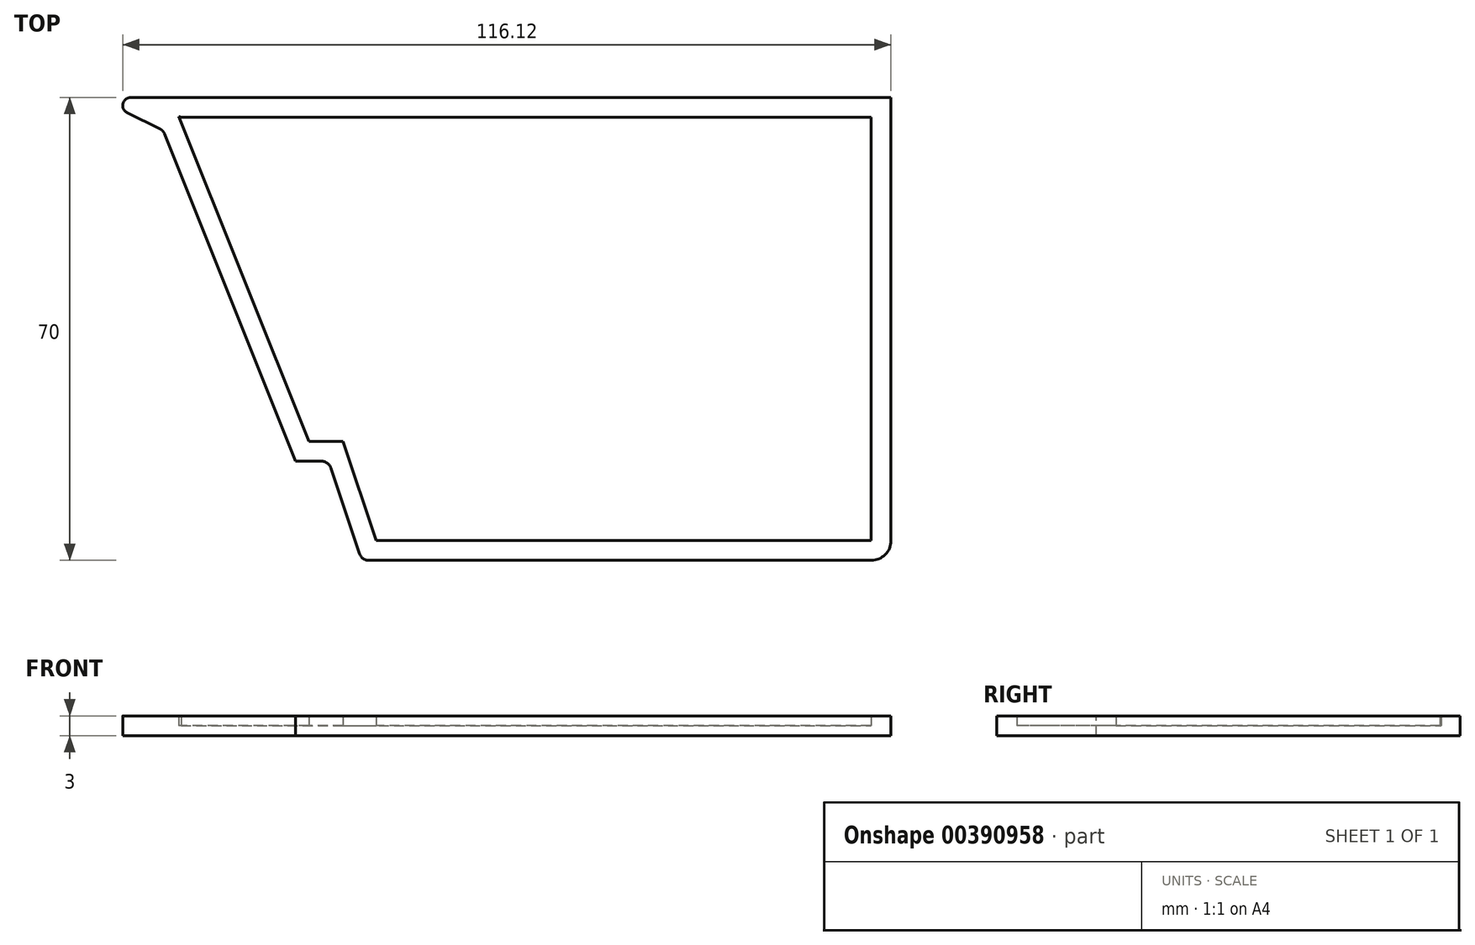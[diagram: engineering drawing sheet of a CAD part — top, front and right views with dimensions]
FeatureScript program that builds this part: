
annotation { "Feature Type Name" : "Feature", "Feature Type Description" : "" }
export const myFeature = defineFeature(function(context is Context, id is Id, definition is map)
    precondition{}
    {
        {
            var Q0;
            Q0=qCreatedBy(makeId("Top.planeOp"),FACE);
            var sketch = newSketch(context, id + "F0", { "sketchPlane" : qUnion([Q0])});
            skLineSegment(sketch, "E0.bottom", {"start": v(40, 35) * mm, "end": v(-40, 35) * mm});
            skLineSegment(sketch, "E0.top", {"start": v(40, -35) * mm, "end": v(-40, -35) * mm});
            skLineSegment(sketch, "E0.left", {"start": v(40, 35) * mm, "end": v(40, -35) * mm});
            skPoint(sketch, "E0.middle", {"position": v(0, 0) * mm});
            skLineSegment(sketch, "E1", {"start": v(-40, -35) * mm, "end": v(-45, -35) * mm, "construction": true});
            skLineSegment(sketch, "E2", {"start": v(-45, -35) * mm, "end": v(-45, -20) * mm, "construction": true});
            skLineSegment(sketch, "E3", {"start": v(-45, -20) * mm, "end": v(-40, -35) * mm});
            skLineSegment(sketch, "E4", {"start": v(-40, -35) * mm, "end": v(-70, -35) * mm, "construction": true});
            skLineSegment(sketch, "E5", {"start": v(-70, -35) * mm, "end": v(-70, 30) * mm, "construction": true});
            skLineSegment(sketch, "E6", {"start": v(-70, -35) * mm, "end": v(-80, -35) * mm, "construction": true});
            skLineSegment(sketch, "E7", {"start": v(-80, -35) * mm, "end": v(-80, 35) * mm, "construction": true});
            skLineSegment(sketch, "E8", {"start": v(-70, 30) * mm, "end": v(-80, 35) * mm});
            skLineSegment(sketch, "E9", {"start": v(-80, 35) * mm, "end": v(-40, 35) * mm});
            skLineSegment(sketch, "E10", {"start": v(-45, -20) * mm, "end": v(-50, -20) * mm});
            skLineSegment(sketch, "E11", {"start": v(-50, -20) * mm, "end": v(-70, 30) * mm});
            skLineSegment(sketch, "E12.0", {"start": v(-42.84, -17) * mm, "end": v(-47.97, -17) * mm});
            skLineSegment(sketch, "E12.1", {"start": v(-42.84, -17) * mm, "end": v(-37.84, -32) * mm});
            skLineSegment(sketch, "E12.2", {"start": v(-47.97, -17) * mm, "end": v(-67.64, 32.17) * mm});
            skLineSegment(sketch, "E12.3", {"start": v(37, -32) * mm, "end": v(-37.84, -32) * mm});
            skLineSegment(sketch, "E12.4", {"start": v(-67.3, 32) * mm, "end": v(-67.64, 32.17) * mm});
            skLineSegment(sketch, "E12.5", {"start": v(-67.3, 32) * mm, "end": v(-40, 32) * mm});
            skLineSegment(sketch, "E12.6", {"start": v(37, 32) * mm, "end": v(-40, 32) * mm});
            skLineSegment(sketch, "E12.7", {"start": v(37, 32) * mm, "end": v(37, -32) * mm});
            skSolve(sketch);
        }
        {
            var Q0;
            Q0=makeQuery(id+"F0.imprint","IMPRINT",FACE,{"disambiguationData":[TD([[makeQuery(id+"F0.imprint","IMPRINT",EDGE,{"derivedFrom":sQuery(id+"F0.wireOp",EDGE,"38467561-a6f7-4828-ac4a-ba29941372dc.0")}),-1.0]])]});
            var Q1;
            Q1=makeQuery(id+"F0.imprint","IMPRINT",FACE,{"disambiguationData":[TD([[makeQuery(id+"F0.imprint","IMPRINT",EDGE,{"derivedFrom":sQuery(id+"F0.wireOp",EDGE,"E0.bottom")}),1.0]])]});
            var Q2;
            Q2=makeQuery(id+"F0.imprint","IMPRINT",FACE,{"disambiguationData":[TD([[makeQuery(id+"F0.imprint","IMPRINT",EDGE,{"derivedFrom":sQuery(id+"F0.wireOp",EDGE,"E12.0")}),-1.0]])]});
            extrude(context, id + "F1", {"entities" : qUnion([Q0, Q1, Q2]), "oppositeDirection" : true, "depth" : 1.5 * mm, "offsetDistance" : 25 * mm});
        }
        {
            var Q0;
            Q0=makeQuery(id+"F0.imprint","IMPRINT",FACE,{"disambiguationData":[TD([[makeQuery(id+"F0.imprint","IMPRINT",EDGE,{"derivedFrom":sQuery(id+"F0.wireOp",EDGE,"E0.bottom")}),1.0]])]});
            extrude(context, id + "F2", {"entities" : qUnion([Q0]), "operationType" : NewBodyOperationType.ADD, "depth" : 1.5 * mm, "offsetDistance" : 25 * mm});
        }
        {
            var Q0;
            {var subQ0=sQuery(id+"F0.wireOp",EDGE,"E9");var subQ1=sQuery(id+"F0.wireOp",EDGE,"E8");Q0=makeQuery(id+"F2.boolean.opBoolean","MERGE",EDGE,{"derivedFrom":[makeQuery(id+"F1.opExtrude","SWEPT_EDGE",EDGE,{"disambiguationData":[OSD([subQ1,subQ0])]}),makeQuery(id+"F2.opExtrude","SWEPT_EDGE",EDGE,{"disambiguationData":[OSD([subQ1,subQ0])]})]});}
            fillet(context, id + "F3", {"entities" : qUnion([Q0]), "radius" : 1.2 * mm, "tangentPropagation" : true, "allowEdgeOverflow" : false});
        }
        {
            var Q0;
            {var subQ0=sQuery(id+"F0.wireOp",EDGE,"E8");var subQ1=sQuery(id+"F0.wireOp",EDGE,"i2pa8zZs-mELL-LkF4-rBhH-qC5wOjDEAE1a");Q0=makeQuery(id+"F2.boolean.opBoolean","MERGE",EDGE,{"derivedFrom":[makeQuery(id+"F1.opExtrude","SWEPT_EDGE",EDGE,{"disambiguationData":[OSD([subQ1,subQ0])]}),makeQuery(id+"F2.opExtrude","SWEPT_EDGE",EDGE,{"disambiguationData":[OSD([subQ1,subQ0])]})]});}
            fillet(context, id + "F4", {"entities" : qUnion([Q0]), "radius" : 1.25 * mm, "tangentPropagation" : true, "allowEdgeOverflow" : false});
        }
        {
            var Q0;
            {var subQ0=sQuery(id+"F0.wireOp",EDGE,"i2pa8zZs-mELL-LkF4-rBhH-qC5wOjDEAE1a");var subQ1=sQuery(id+"F0.wireOp",EDGE,"E3");Q0=makeQuery(id+"F2.boolean.opBoolean","MERGE",EDGE,{"derivedFrom":[makeQuery(id+"F1.opExtrude","SWEPT_EDGE",EDGE,{"disambiguationData":[OSD([subQ1,subQ0])]}),makeQuery(id+"F2.opExtrude","SWEPT_EDGE",EDGE,{"disambiguationData":[OSD([subQ1,subQ0])]})]});}
            fillet(context, id + "F5", {"entities" : qUnion([Q0]), "radius" : 1.5 * mm, "tangentPropagation" : true, "allowEdgeOverflow" : false});
        }
        {
            var Q0;
            {var subQ0=sQuery(id+"F0.wireOp",EDGE,"E3");var subQ1=sQuery(id+"F0.wireOp",EDGE,"E0.top");Q0=makeQuery(id+"F2.boolean.opBoolean","MERGE",EDGE,{"derivedFrom":[makeQuery(id+"F1.opExtrude","SWEPT_EDGE",EDGE,{"disambiguationData":[OSD([subQ1,subQ0])]}),makeQuery(id+"F2.opExtrude","SWEPT_EDGE",EDGE,{"disambiguationData":[OSD([subQ1,subQ0])]})]});}
            var Q1;
            {var subQ0=sQuery(id+"F0.wireOp",EDGE,"E0.left");var subQ1=sQuery(id+"F0.wireOp",EDGE,"E0.top");Q1=makeQuery(id+"F2.boolean.opBoolean","MERGE",EDGE,{"derivedFrom":[makeQuery(id+"F1.opExtrude","SWEPT_EDGE",EDGE,{"disambiguationData":[OSD([subQ1,subQ0])]}),makeQuery(id+"F2.opExtrude","SWEPT_EDGE",EDGE,{"disambiguationData":[OSD([subQ1,subQ0])]})]});}
            fillet(context, id + "F6", {"entities" : qUnion([Q0, Q1]), "radius" : 3 * mm, "tangentPropagation" : true, "allowEdgeOverflow" : false});
        }
    });
